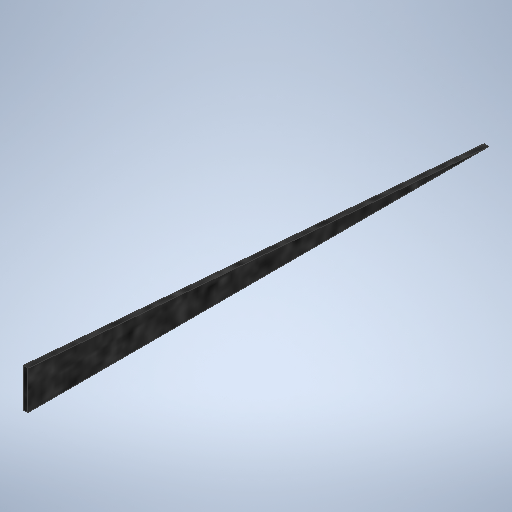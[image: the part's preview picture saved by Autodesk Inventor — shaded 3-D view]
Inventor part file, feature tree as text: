
AUTODESK INVENTOR PART (.ipt)
format: ipt  version: 2025.1 (Build 291241020, 241B)  size: 259,584 bytes
history: native  units: in
note: dims shown in document units (in); Inventor stores cm internally (conversion verified against a paired STEP export)
features: extrude x1, sketch x1
ambient origin geometry x8: Origin, YZ Plane, XZ Plane, XY Plane, X Axis, Y Axis, Z Axis, Center Point
bodies: Solid1 (feature_tree)
feature tree (2):
  extrude  "Extrusion1"  Depth=12.0in
  sketch  "Sketch1"  dims[d0=1.0in d1=12.0in d2=0.125in d3=0.0in]
